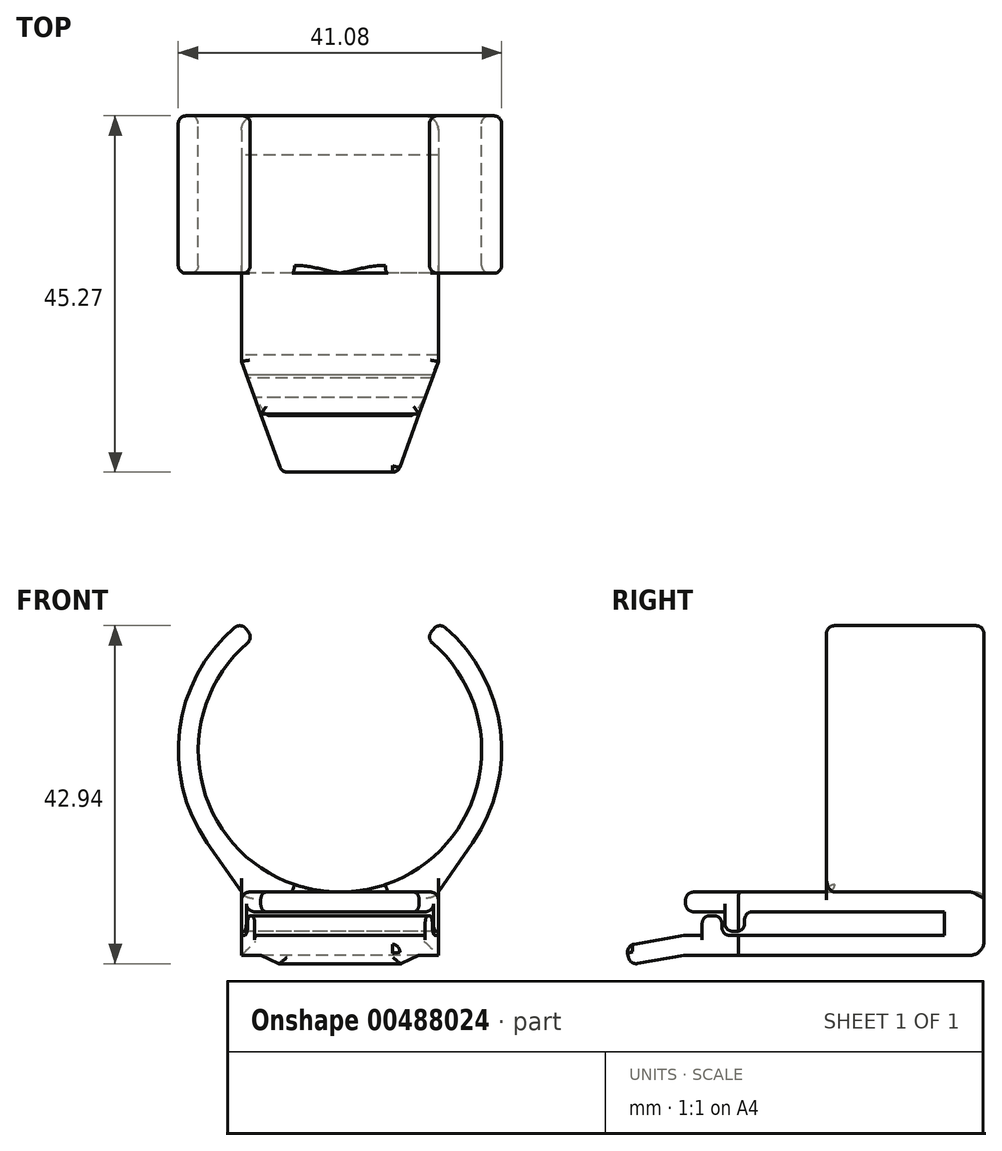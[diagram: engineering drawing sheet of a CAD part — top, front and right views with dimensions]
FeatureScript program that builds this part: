
annotation { "Feature Type Name" : "Feature", "Feature Type Description" : "" }
export const myFeature = defineFeature(function(context is Context, id is Id, definition is map)
    precondition{}
    {
        {
            var Q0;
            Q0=qCreatedBy(makeId("Right.planeOp"),FACE);
            var sketch = newSketch(context, id + "F0", { "sketchPlane" : qUnion([Q0])});
            skLineSegment(sketch, "E0.bottom", {"start": v(0, 0) * mm, "end": v(-38.1, 0) * mm});
            skLineSegment(sketch, "E0.top", {"start": v(-5, 2.54) * mm, "end": v(-33.3, 2.54) * mm});
            skLineSegment(sketch, "E0.left", {"start": v(0, 0) * mm, "end": v(0, 2.54) * mm});
            skLineSegment(sketch, "E1", {"start": v(-38.1, 0) * mm, "end": v(-45, -1.22) * mm});
            skLineSegment(sketch, "E2", {"start": v(-45, -1.22) * mm, "end": v(-45.43, 1.25) * mm});
            skLineSegment(sketch, "E3", {"start": v(-38.1, 2.54) * mm, "end": v(-45.43, 1.25) * mm});
            skLineSegment(sketch, "E4", {"start": v(-35.43, 0) * mm, "end": v(-38.1, 0) * mm, "construction": true});
            skLineSegment(sketch, "E5", {"start": v(-38.1, 0) * mm, "end": v(-38.1, 2.54) * mm, "construction": true});
            skLineSegment(sketch, "E6.top", {"start": v(0, 8.04) * mm, "end": v(0, 8.04) * mm});
            skLineSegment(sketch, "E6.left", {"start": v(0, 2.54) * mm, "end": v(0, 8.04) * mm});
            skLineSegment(sketch, "E6.right", {"start": v(-5, 2.54) * mm, "end": v(-5, 5.54) * mm});
            skLineSegment(sketch, "E7.bottom", {"start": v(0, 8.04) * mm, "end": v(-37.9, 8.04) * mm});
            skLineSegment(sketch, "E7.top", {"start": v(-5, 5.54) * mm, "end": v(-30.4, 5.54) * mm});
            skLineSegment(sketch, "E7.right", {"start": v(-37.9, 8.04) * mm, "end": v(-37.9, 5.54) * mm});
            skLineSegment(sketch, "E8.top", {"start": v(-32.9, 3.04) * mm, "end": v(-30.4, 3.04) * mm});
            skLineSegment(sketch, "E8.left", {"start": v(-32.9, 5.54) * mm, "end": v(-32.9, 3.04) * mm});
            skLineSegment(sketch, "E8.right", {"start": v(-30.4, 5.54) * mm, "end": v(-30.4, 3.04) * mm});
            skLineSegment(sketch, "E9.trimOffspring", {"start": v(-32.9, 5.54) * mm, "end": v(-37.9, 5.54) * mm});
            skLineSegment(sketch, "E10", {"start": v(-33.3, 2.54) * mm, "end": v(-33.3, 5.04) * mm});
            skLineSegment(sketch, "E11", {"start": v(-33.3, 5.04) * mm, "end": v(-35.8, 5.04) * mm});
            skLineSegment(sketch, "E12", {"start": v(-35.8, 5.04) * mm, "end": v(-35.8, 2.54) * mm});
            skLineSegment(sketch, "E13.trimOffspring", {"start": v(-35.8, 2.54) * mm, "end": v(-38.1, 2.54) * mm});
            skSolve(sketch);
        }
        {
            var Q0;
            Q0=qSketchRegion(id+"F0",true);
            extrude(context, id + "F1", {"entities" : qUnion([Q0]), "depth" : 25 * mm});
        }
        {
            var Q0;
            Q0=makeQuery(id+"F1.opExtrude","SWEPT_FACE",FACE,{"disambiguationData":[OSD([sQuery(id+"F0.wireOp",EDGE,"E0.left"),sQuery(id+"F0.wireOp",EDGE,"E6.left")])]});
            var sketch = newSketch(context, id + "F2", { "sketchPlane" : qUnion([Q0])});
            skLineSegment(sketch, "E14", {"start": v(-12.5, 8.04) * mm, "end": v(-12.5, 44.73) * mm, "construction": true});
            skArc(sketch, "E15", {"start": v(-24.23, 39.69) * mm, "mid": v(-12.5, 8.04) * mm, "end": v(-0.77, 39.69) * mm});
            skLineSegment(sketch, "E16", {"start": v(-12.5, 8.04) * mm, "end": v(0, 8.04) * mm, "construction": true});
            skArc(sketch, "E17.0", {"start": v(4.36, 14.31) * mm, "mid": v(7.87, 28.65) * mm, "end": v(0.87, 41.63) * mm});
            skLineSegment(sketch, "E18", {"start": v(-25, 8.04) * mm, "end": v(0, 8.04) * mm});
            skLineSegment(sketch, "E19", {"start": v(0, 8.04) * mm, "end": v(4.36, 14.31) * mm});
            skLineSegment(sketch, "E20", {"start": v(-25, 8.04) * mm, "end": v(-29.36, 14.31) * mm});
            skLineSegment(sketch, "E21", {"start": v(-0.9, 41.06) * mm, "end": v(-0.57, 41.49) * mm});
            skPoint(sketch, "E22", {"position": v(-1.5, 40.29) * mm});
            skLineSegment(sketch, "E23.MirrorCS", {"start": v(-24.1, 41.06) * mm, "end": v(-24.43, 41.49) * mm});
            skArc(sketch, "E24.trimOffspring", {"start": v(-25.87, 41.63) * mm, "mid": v(-32.87, 28.65) * mm, "end": v(-29.36, 14.31) * mm});
            skPoint(sketch, "E25.visualSharp", {"position": v(-23.5, 40.29) * mm});
            skArc(sketch, "E25.filletArc", {"start": v(-24.23, 39.69) * mm, "mid": v(-23.9, 40.35) * mm, "end": v(-24.1, 41.06) * mm});
            skPoint(sketch, "E26.visualSharp", {"position": v(-25.05, 42.3) * mm});
            skArc(sketch, "E26.filletArc", {"start": v(-24.43, 41.49) * mm, "mid": v(-25.11, 41.87) * mm, "end": v(-25.87, 41.63) * mm});
            skArc(sketch, "E27.filletArc", {"start": v(-0.9, 41.06) * mm, "mid": v(-1.1, 40.35) * mm, "end": v(-0.77, 39.69) * mm});
            skPoint(sketch, "E28.visualSharp", {"position": v(0.05, 42.3) * mm});
            skArc(sketch, "E28.filletArc", {"start": v(0.87, 41.63) * mm, "mid": v(0.11, 41.87) * mm, "end": v(-0.57, 41.49) * mm});
            skSolve(sketch);
        }
        {
            var Q0;
            Q0=qSketchRegion(id+"F2",true);
            extrude(context, id + "F3", {"entities" : qUnion([Q0]), "operationType" : NewBodyOperationType.ADD, "oppositeDirection" : true, "depth" : 20 * mm});
        }
        {
            var Q0;
            Q0=makeQuery(id+"F1.opExtrude","SWEPT_FACE",FACE,{"disambiguationData":[OSD([sQuery(id+"F0.wireOp",EDGE,"E0.bottom")])]});
            var sketch = newSketch(context, id + "F4", { "sketchPlane" : qUnion([Q0])});
            skLineSegment(sketch, "E29", {"start": v(12.5, 0) * mm, "end": v(12.5, 56.84) * mm, "construction": true});
            skLineSegment(sketch, "E30", {"start": v(12.5, 45.55) * mm, "end": v(19.78, 45.55) * mm});
            skLineSegment(sketch, "E31", {"start": v(19.78, 45.55) * mm, "end": v(26.83, 26.17) * mm});
            skLineSegment(sketch, "E32", {"start": v(26.83, 26.17) * mm, "end": v(31.87, 26.17) * mm});
            skLineSegment(sketch, "E33", {"start": v(31.87, 26.17) * mm, "end": v(31.87, 54.4) * mm});
            skLineSegment(sketch, "E34", {"start": v(31.87, 54.4) * mm, "end": v(12.5, 54.4) * mm});
            skLineSegment(sketch, "E35.MirrorCS", {"start": v(-6.87, 54.4) * mm, "end": v(12.5, 54.4) * mm});
            skLineSegment(sketch, "E36.MirrorCS", {"start": v(-6.87, 26.17) * mm, "end": v(-6.87, 54.4) * mm});
            skLineSegment(sketch, "E37.MirrorCS", {"start": v(-1.83, 26.17) * mm, "end": v(-6.87, 26.17) * mm});
            skLineSegment(sketch, "E38.MirrorCS", {"start": v(12.5, 45.55) * mm, "end": v(5.22, 45.55) * mm});
            skLineSegment(sketch, "E39.MirrorCS", {"start": v(5.22, 45.55) * mm, "end": v(-1.83, 26.17) * mm});
            skSolve(sketch);
        }
        {
            var Q0;
            Q0=qSketchRegion(id+"F4",true);
            extrude(context, id + "F5", {"entities" : qUnion([Q0]), "operationType" : NewBodyOperationType.REMOVE, "oppositeDirection" : true, "depth" : 25 * mm, "hasSecondDirection" : true, "secondDirectionOppositeDirection" : false, "secondDirectionDepth" : 25 * mm});
        }
        {
            var Q0;
            Q0=makeQuery(id+"F1.opExtrude","SWEPT_EDGE",EDGE,{"disambiguationData":[OSD([sQuery(id+"F0.wireOp",EDGE,"E2"),sQuery(id+"F0.wireOp",EDGE,"E3")])]});
            var Q1;
            Q1=makeQuery(id+"F1.opExtrude","SWEPT_EDGE",EDGE,{"disambiguationData":[OSD([sQuery(id+"F0.wireOp",EDGE,"E1"),sQuery(id+"F0.wireOp",EDGE,"E2")])]});
            var Q2;
            Q2=makeQuery(id+"F5.boolean.opBoolean","INTERSECT",EDGE,{"derivedFrom":[makeQuery(id+"F1.opExtrude","SWEPT_FACE",FACE,{"disambiguationData":[OSD([sQuery(id+"F0.wireOp",EDGE,"E2")])]}),makeQuery(id+"F5.opExtrude","SWEPT_FACE",FACE,{"disambiguationData":[OSD([sQuery(id+"F4.wireOp",EDGE,"E39.MirrorCS")])]})]});
            var Q3;
            Q3=makeQuery(id+"F5.boolean.opBoolean","INTERSECT",EDGE,{"derivedFrom":[makeQuery(id+"F1.opExtrude","SWEPT_FACE",FACE,{"disambiguationData":[OSD([sQuery(id+"F0.wireOp",EDGE,"E2")])]}),makeQuery(id+"F5.opExtrude","SWEPT_FACE",FACE,{"disambiguationData":[OSD([sQuery(id+"F4.wireOp",EDGE,"E31")])]})]});
            var Q4;
            Q4=makeQuery(id+"F5.boolean.opBoolean","INTERSECT",EDGE,{"derivedFrom":[makeQuery(id+"F1.opExtrude","SWEPT_FACE",FACE,{"disambiguationData":[OSD([sQuery(id+"F0.wireOp",EDGE,"E3")])]}),makeQuery(id+"F5.opExtrude","SWEPT_FACE",FACE,{"disambiguationData":[OSD([sQuery(id+"F4.wireOp",EDGE,"E31")])]})]});
            var Q5;
            Q5=makeQuery(id+"F1.opExtrude","SWEPT_EDGE",EDGE,{"disambiguationData":[OSD([sQuery(id+"F0.wireOp",EDGE,"E7.bottom"),sQuery(id+"F0.wireOp",EDGE,"E7.right")])]});
            var Q6;
            Q6=makeQuery(id+"F5.boolean.opBoolean","INTERSECT",EDGE,{"derivedFrom":[makeQuery(id+"F1.opExtrude","SWEPT_FACE",FACE,{"disambiguationData":[OSD([sQuery(id+"F0.wireOp",EDGE,"E3")])]}),makeQuery(id+"F5.opExtrude","SWEPT_FACE",FACE,{"disambiguationData":[OSD([sQuery(id+"F4.wireOp",EDGE,"E39.MirrorCS")])]})]});
            var Q7;
            Q7=makeQuery(id+"F3.boolean.opBoolean","SPLIT",EDGE,{"derivedFrom":makeQuery(id+"F1.opExtrude","CAP_EDGE",EDGE,{"disambiguationData":[OSD([sQuery(id+"F0.wireOp",EDGE,"E7.bottom")])],"isStart":true})});
            var Q8;
            Q8=makeQuery(id+"F3.boolean.opBoolean","SPLIT",EDGE,{"derivedFrom":makeQuery(id+"F1.opExtrude","CAP_EDGE",EDGE,{"disambiguationData":[OSD([sQuery(id+"F0.wireOp",EDGE,"E7.bottom")])],"isStart":false})});
            var Q9;
            Q9=makeQuery(id+"F5.boolean.opBoolean","INTERSECT",EDGE,{"derivedFrom":[makeQuery(id+"F1.opExtrude","SWEPT_FACE",FACE,{"disambiguationData":[OSD([sQuery(id+"F0.wireOp",EDGE,"E7.bottom")])]}),makeQuery(id+"F5.opExtrude","SWEPT_FACE",FACE,{"disambiguationData":[OSD([sQuery(id+"F4.wireOp",EDGE,"E31")])]})]});
            var Q10;
            Q10=makeQuery(id+"F5.boolean.opBoolean","INTERSECT",EDGE,{"derivedFrom":[makeQuery(id+"F1.opExtrude","SWEPT_FACE",FACE,{"disambiguationData":[OSD([sQuery(id+"F0.wireOp",EDGE,"E7.bottom")])]}),makeQuery(id+"F5.opExtrude","SWEPT_FACE",FACE,{"disambiguationData":[OSD([sQuery(id+"F4.wireOp",EDGE,"E39.MirrorCS")])]})]});
            fillet(context, id + "F6", {"entities" : qUnion([Q0, Q1, Q2, Q3, Q4, Q5, Q6, Q7, Q8, Q9, Q10]), "radius" : 1 * mm, "tangentPropagation" : true, "allowEdgeOverflow" : false});
        }
        {
            var Q0;
            {var subQ0=sQuery(id+"F2.wireOp",EDGE,"E15");Q0=makeQuery(id+"F3.boolean.opBoolean","MERGE",EDGE,{"derivedFrom":[makeQuery(id+"F3.opExtrude","CAP_EDGE",EDGE,{"disambiguationData":[OSD([subQ0]),TDD([makeQuery(id+"F2.imprint","IMPRINT",EDGE,{"disambiguationData":[TD([[makeQuery(id+"F2.imprint","INTERSECT",VERTEX,{"derivedFrom":[subQ0,sQuery(id+"F2.wireOp",EDGE,"E25.filletArc")]}),-1.0]])],"derivedFrom":subQ0})])],"isStart":true}),makeQuery(id+"F3.opExtrude","CAP_EDGE",EDGE,{"disambiguationData":[OSD([subQ0]),TDD([makeQuery(id+"F2.imprint","IMPRINT",EDGE,{"disambiguationData":[TD([[makeQuery(id+"F2.imprint","INTERSECT",VERTEX,{"derivedFrom":[subQ0,sQuery(id+"F2.wireOp",EDGE,"E27.filletArc")]}),1.0]])],"derivedFrom":subQ0})])],"isStart":true})]});}
            var Q1;
            {var subQ0=sQuery(id+"F2.wireOp",EDGE,"E15");Q1=makeQuery(id+"F3.opExtrude","CAP_EDGE",EDGE,{"disambiguationData":[OSD([subQ0]),TDD([makeQuery(id+"F2.imprint","IMPRINT",EDGE,{"disambiguationData":[TD([[makeQuery(id+"F2.imprint","INTERSECT",VERTEX,{"derivedFrom":[subQ0,sQuery(id+"F2.wireOp",EDGE,"E25.filletArc")]}),-1.0]])],"derivedFrom":subQ0})])],"isStart":false});}
            fillet(context, id + "F7", {"entities" : qUnion([Q0, Q1]), "radius" : 1 * mm, "tangentPropagation" : true, "allowEdgeOverflow" : false});
        }
        {
            var Q0;
            Q0=makeQuery(id+"F1.opExtrude","CAP_EDGE",EDGE,{"disambiguationData":[OSD([sQuery(id+"F0.wireOp",EDGE,"E0.left"),sQuery(id+"F0.wireOp",EDGE,"E6.left")])],"isStart":false});
            var Q1;
            Q1=makeQuery(id+"F1.opExtrude","SWEPT_EDGE",EDGE,{"disambiguationData":[OSD([sQuery(id+"F0.wireOp",EDGE,"E0.bottom"),sQuery(id+"F0.wireOp",EDGE,"E0.left")])]});
            var Q2;
            Q2=makeQuery(id+"F1.opExtrude","CAP_EDGE",EDGE,{"disambiguationData":[OSD([sQuery(id+"F0.wireOp",EDGE,"E0.left"),sQuery(id+"F0.wireOp",EDGE,"E6.left")])],"isStart":true});
            fillet(context, id + "F8", {"entities" : qUnion([Q0, Q1, Q2]), "radius" : 1.8 * mm, "tangentPropagation" : true, "allowEdgeOverflow" : false});
        }
        {
            var Q0;
            Q0=makeQuery(id+"F1.opExtrude","SWEPT_EDGE",EDGE,{"disambiguationData":[OSD([sQuery(id+"F0.wireOp",EDGE,"E7.right"),sQuery(id+"F0.wireOp",EDGE,"E9.trimOffspring")])]});
            var Q1;
            Q1=makeQuery(id+"F5.boolean.opBoolean","INTERSECT",EDGE,{"derivedFrom":[makeQuery(id+"F1.opExtrude","SWEPT_FACE",FACE,{"disambiguationData":[OSD([sQuery(id+"F0.wireOp",EDGE,"E9.trimOffspring")])]}),makeQuery(id+"F5.opExtrude","SWEPT_FACE",FACE,{"disambiguationData":[OSD([sQuery(id+"F4.wireOp",EDGE,"E31")])]})]});
            var Q2;
            Q2=makeQuery(id+"F5.boolean.opBoolean","INTERSECT",EDGE,{"derivedFrom":[makeQuery(id+"F1.opExtrude","SWEPT_FACE",FACE,{"disambiguationData":[OSD([sQuery(id+"F0.wireOp",EDGE,"E9.trimOffspring")])]}),makeQuery(id+"F5.opExtrude","SWEPT_FACE",FACE,{"disambiguationData":[OSD([sQuery(id+"F4.wireOp",EDGE,"E39.MirrorCS")])]})]});
            fillet(context, id + "F9", {"entities" : qUnion([Q0, Q1, Q2]), "radius" : 1 * mm, "tangentPropagation" : true, "allowEdgeOverflow" : false});
        }
        {
            var Q0;
            Q0=makeQuery(id+"F1.opExtrude","SWEPT_EDGE",EDGE,{"disambiguationData":[OSD([sQuery(id+"F0.wireOp",EDGE,"E10"),sQuery(id+"F0.wireOp",EDGE,"E11")])]});
            var Q1;
            Q1=makeQuery(id+"F1.opExtrude","SWEPT_EDGE",EDGE,{"disambiguationData":[OSD([sQuery(id+"F0.wireOp",EDGE,"E8.top"),sQuery(id+"F0.wireOp",EDGE,"E8.right")])]});
            var Q2;
            Q2=makeQuery(id+"F1.opExtrude","SWEPT_EDGE",EDGE,{"disambiguationData":[OSD([sQuery(id+"F0.wireOp",EDGE,"E8.top"),sQuery(id+"F0.wireOp",EDGE,"E8.left")])]});
            var Q3;
            Q3=makeQuery(id+"F1.opExtrude","SWEPT_EDGE",EDGE,{"disambiguationData":[OSD([sQuery(id+"F0.wireOp",EDGE,"E11"),sQuery(id+"F0.wireOp",EDGE,"E12")])]});
            var Q4;
            Q4=makeQuery(id+"F1.opExtrude","SWEPT_EDGE",EDGE,{"disambiguationData":[OSD([sQuery(id+"F0.wireOp",EDGE,"E0.top"),sQuery(id+"F0.wireOp",EDGE,"E10")])]});
            var Q5;
            Q5=makeQuery(id+"F1.opExtrude","SWEPT_EDGE",EDGE,{"disambiguationData":[OSD([sQuery(id+"F0.wireOp",EDGE,"E7.top"),sQuery(id+"F0.wireOp",EDGE,"E8.right")])]});
            fillet(context, id + "F10", {"entities" : qUnion([Q0, Q1, Q2, Q3, Q4, Q5]), "radius" : 1 * mm, "tangentPropagation" : true, "allowEdgeOverflow" : false});
        }
    });
